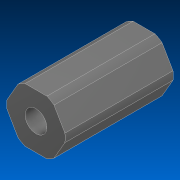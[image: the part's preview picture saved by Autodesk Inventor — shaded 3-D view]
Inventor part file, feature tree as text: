
AUTODESK INVENTOR PART (.ipt)
format: ipt  version: 2022.2 (Build 262287000, 287)  size: 126,464 bytes
history: native  units: in
note: dims shown in document units (in); Inventor stores cm internally (conversion verified against a paired STEP export)
features: extrude x1, sketch x1, other x1
ambient origin geometry x8: Origin, YZ Plane, XZ Plane, XY Plane, X Axis, Y Axis, Z Axis, Center Point
bodies: Solid1 (feature_tree)
feature tree (3):
  extrude  "Extrusion1"  TaperAngle=0.0deg  [1 undecoded]
  sketch  "Sketch1"  dims[d0=35.0in d1=0.0in]
  other  "Cut-Extrude2"
note: 1 required parameter value undecoded (feature->parameter linkage not recoverable at this tier; creation-order binding heuristic only, values carry confidence <= 0.55)
